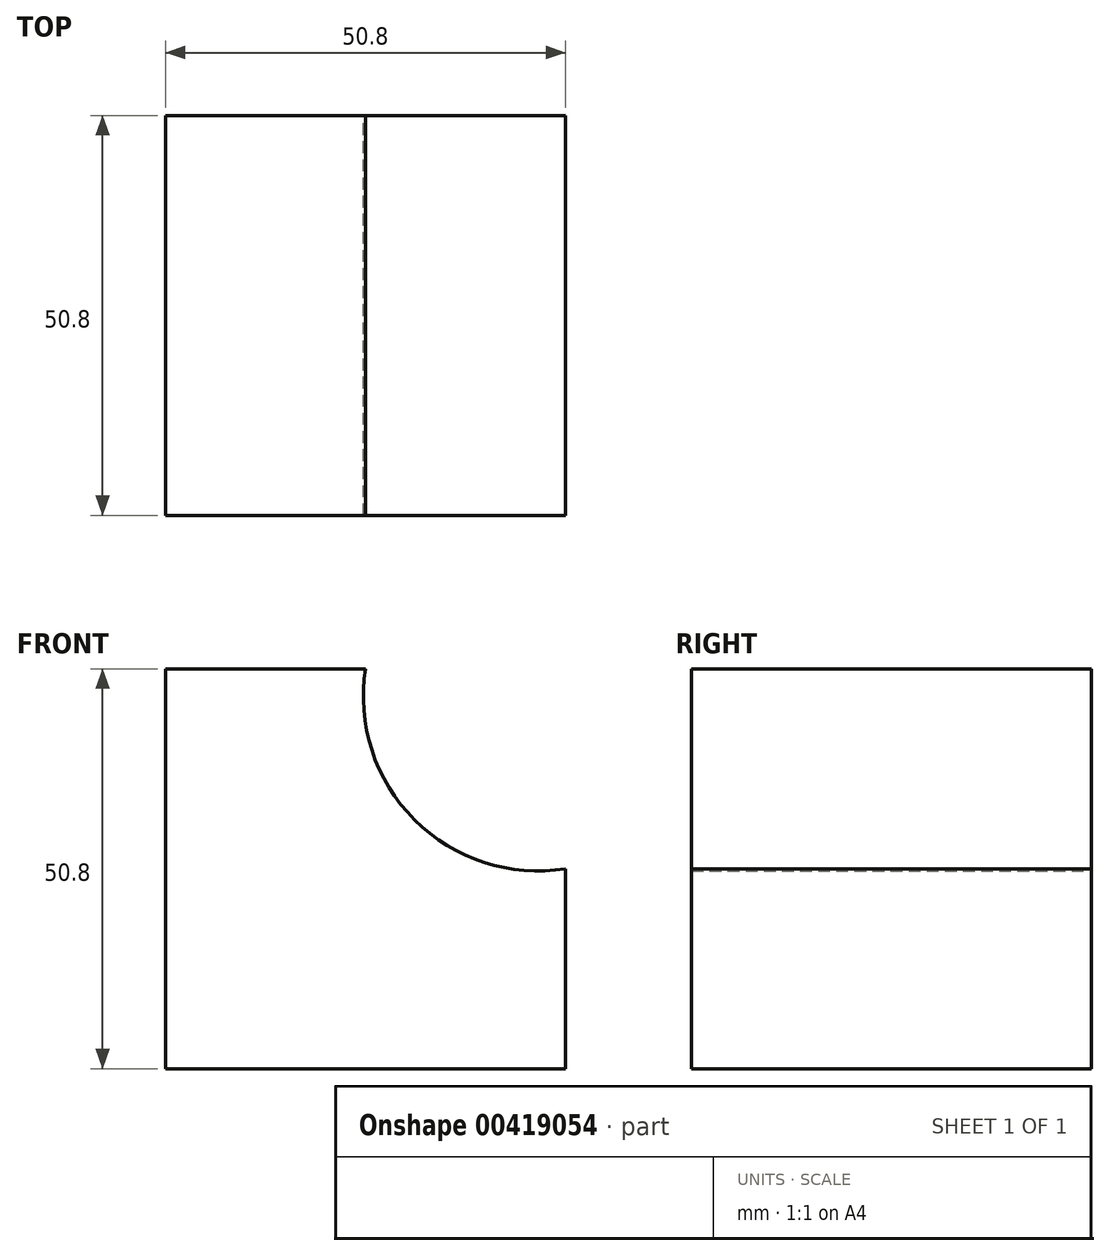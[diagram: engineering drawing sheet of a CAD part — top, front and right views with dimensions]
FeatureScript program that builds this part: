
annotation { "Feature Type Name" : "Feature", "Feature Type Description" : "" }
export const myFeature = defineFeature(function(context is Context, id is Id, definition is map)
    precondition{}
    {
        {
            var Q0;
            Q0=qCreatedBy(makeId("Front.planeOp"),FACE);
            var sketch = newSketch(context, id + "F0", { "sketchPlane" : qUnion([Q0])});
            skLineSegment(sketch, "E0", {"start": v(0, 0) * mm, "end": v(-50.8, 0) * mm});
            skLineSegment(sketch, "E1", {"start": v(-50.8, 0) * mm, "end": v(-50.8, 50.8) * mm});
            skLineSegment(sketch, "E2", {"start": v(-50.8, 50.8) * mm, "end": v(-25.4, 50.8) * mm});
            skLineSegment(sketch, "E3", {"start": v(0, 0) * mm, "end": v(0, 25.4) * mm});
            skArc(sketch, "E4", {"start": v(-25.4, 50.8) * mm, "mid": v(-19.18, 31.62) * mm, "end": v(0, 25.4) * mm});
            skSolve(sketch);
        }
        {
            var Q0;
            Q0 = qSketchRegion(id + "F0", true);
            extrude(context, id + "F1", {"entities" : qUnion([Q0]), "depth" : 50.8 * mm});
        }
    });
